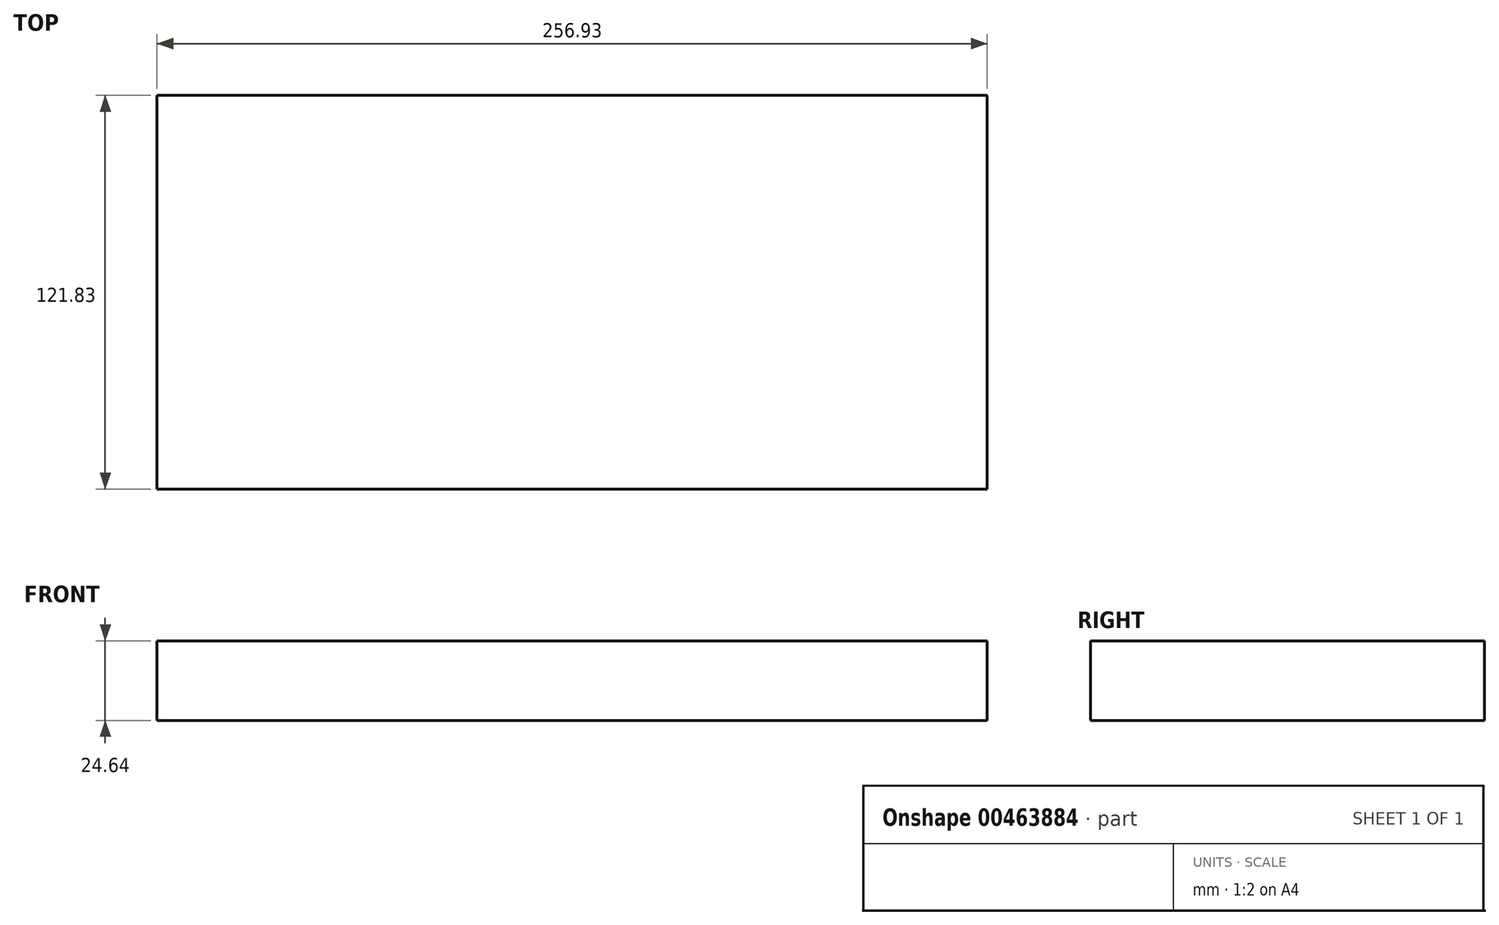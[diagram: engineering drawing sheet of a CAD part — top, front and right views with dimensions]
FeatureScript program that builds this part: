
annotation { "Feature Type Name" : "Feature", "Feature Type Description" : "" }
export const myFeature = defineFeature(function(context is Context, id is Id, definition is map)
    precondition{}
    {
        {
            var Q0;
            Q0=qCreatedBy(makeId("Top.planeOp"),FACE);
            var sketch = newSketch(context, id + "F0", { "sketchPlane" : qUnion([Q0])});
            skLineSegment(sketch, "E0.bottom", {"start": v(-129.77, -50.28) * mm, "end": v(127.16, -50.28) * mm});
            skLineSegment(sketch, "E0.top", {"start": v(-129.77, 71.55) * mm, "end": v(127.16, 71.55) * mm});
            skLineSegment(sketch, "E0.left", {"start": v(-129.77, -50.28) * mm, "end": v(-129.77, 71.55) * mm});
            skLineSegment(sketch, "E0.right", {"start": v(127.16, -50.28) * mm, "end": v(127.16, 71.55) * mm});
            skSolve(sketch);
        }
        {
            var Q0;
            Q0=makeQuery(id+"F0.imprint","IMPRINT",FACE,{"disambiguationData":[TD([[makeQuery(id+"F0.imprint","IMPRINT",EDGE,{"derivedFrom":sQuery(id+"F0.wireOp",EDGE,"E0.bottom")}),1.0]])]});
            extrude(context, id + "F1", {"entities" : qUnion([Q0]), "depth" : 24.64 * mm});
        }
    });
